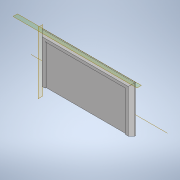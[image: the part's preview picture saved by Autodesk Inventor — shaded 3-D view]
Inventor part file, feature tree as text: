
AUTODESK INVENTOR PART (.ipt)
format: ipt  version: 2022 (Build 260153000, 153)  size: 118,272 bytes
history: native  units: mm
features: plane x2, sketch x2, extrude x2, other x1, chamfer x1
ambient origin geometry x8: Origin, YZ Plane, XZ Plane, XY Plane, X Axis, Y Axis, Z Axis, Center Point
bodies: Solid1 (feature_tree)
feature tree (8):
  plane  "Work Plane1"
  sketch  "Sketch2"  dims[d8=0.0mm d9=9.525mm d10=45.0deg d11=2.0mm d12=10.16mm d13=90.0deg d16=90.0deg d17=88.9mm]
  other  "Work Axis1"
  plane  "Work Plane2"
  sketch  "Sketch1"  dims[d0=19.05mm d1=19.05mm d2=254.0mm d3=127.0mm d5=0.0mm d6=12.7mm]
  chamfer  "Chamfer1"  Angle=90.0deg  [1 undecoded]
  extrude  "Extrusion1"  Depth=9.525mm TaperAngle=90.0deg
  extrude  "Extrusion2"  [1 undecoded]
note: 2 required parameter values undecoded (feature->parameter linkage not recoverable at this tier; creation-order binding heuristic only, values carry confidence <= 0.55)
